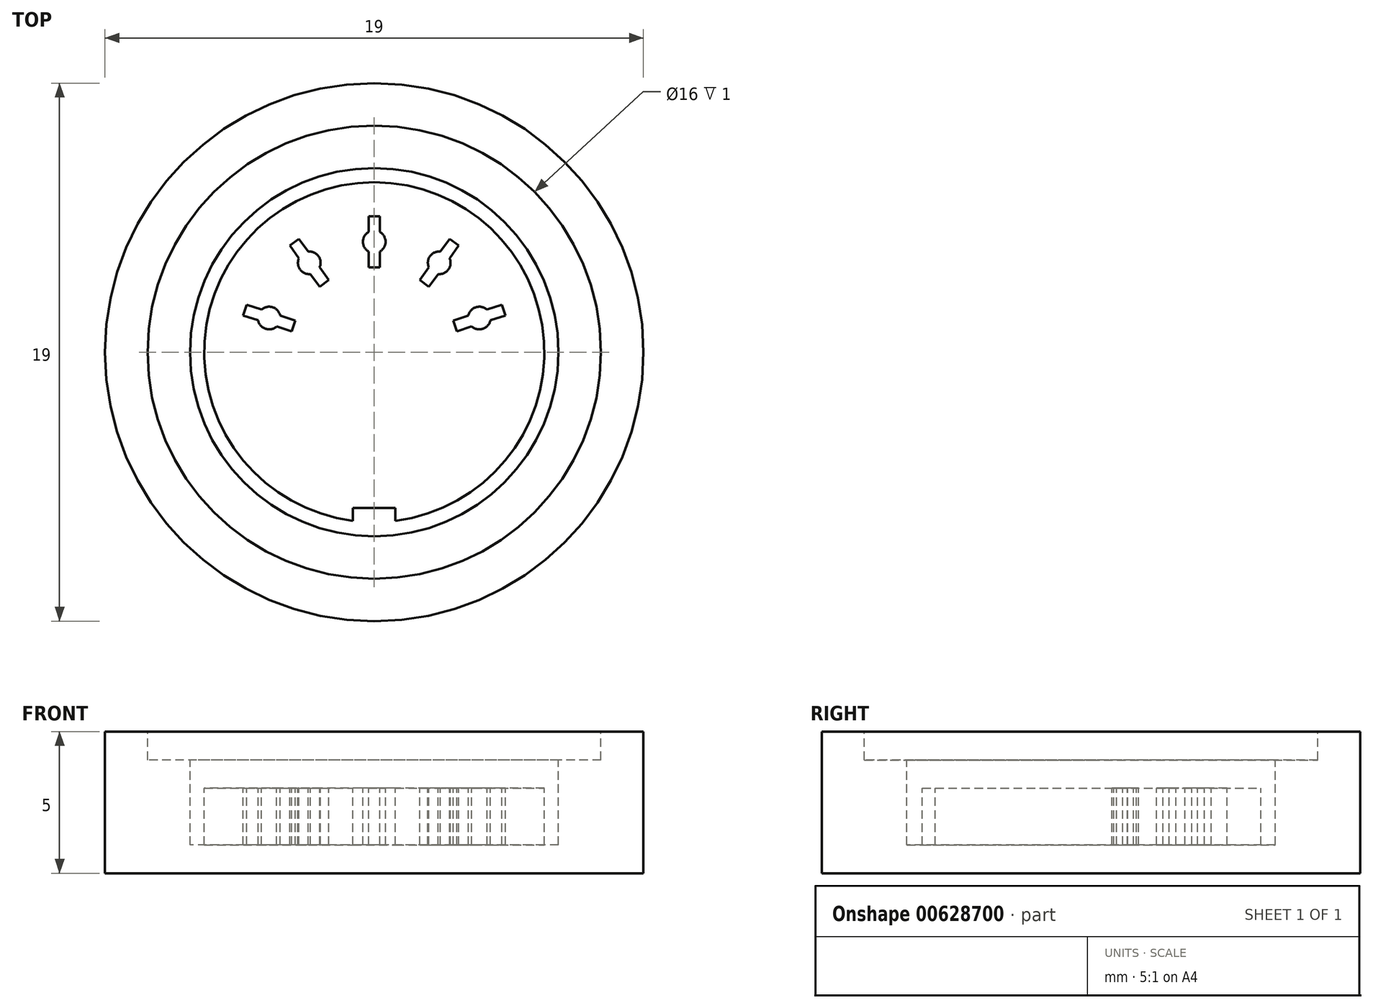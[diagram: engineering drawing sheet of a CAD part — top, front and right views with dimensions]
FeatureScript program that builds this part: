
annotation { "Feature Type Name" : "Feature", "Feature Type Description" : "" }
export const myFeature = defineFeature(function(context is Context, id is Id, definition is map)
    precondition{}
    {
        {
            var Q0;
            Q0=qCreatedBy(makeId("Top.planeOp"),FACE);
            var sketch = newSketch(context, id + "F0", { "sketchPlane" : qUnion([Q0])});
            skCircle(sketch, "E0", {"center": v(0, 0) * mm, "radius": 9.5 * mm});
            skSolve(sketch);
        }
        {
            var Q0;
            Q0 = qSketchRegion(id + "F0", true);
            extrude(context, id + "F1", {"entities" : qUnion([Q0]), "endBound" : BoundingType.SYMMETRIC, "depth" : 5 * mm, "offsetDistance" : 25 * mm});
        }
        {
            var Q0;
            Q0=makeQuery(id+"F1.opExtrude","CAP_FACE",FACE,{"disambiguationData":[OSD([sQuery(id+"F0.wireOp",EDGE,"E0")])],"isStart":false});
            var sketch = newSketch(context, id + "F2", { "sketchPlane" : qUnion([Q0])});
            skCircle(sketch, "E1", {"center": v(0, 0) * mm, "radius": 6.5 * mm});
            skArc(sketch, "E2", {"start": v(0.75, -5.95) * mm, "mid": v(0, 6) * mm, "end": v(-0.75, -5.95) * mm});
            skLineSegment(sketch, "E3", {"start": v(-0.75, -5.95) * mm, "end": v(-0.75, -5.5) * mm});
            skLineSegment(sketch, "E4", {"start": v(-0.75, -5.5) * mm, "end": v(0.75, -5.5) * mm});
            skLineSegment(sketch, "E5", {"start": v(0.75, -5.5) * mm, "end": v(0.75, -5.95) * mm});
            skLineSegment(sketch, "E6.bottom", {"start": v(0.2, 3) * mm, "end": v(-0.2, 3) * mm});
            skLineSegment(sketch, "E6.top", {"start": v(0.2, 4.8) * mm, "end": v(-0.2, 4.8) * mm});
            skLineSegment(sketch, "E6.left", {"start": v(0.2, 3) * mm, "end": v(0.2, 3.55) * mm});
            skLineSegment(sketch, "E6.right", {"start": v(-0.2, 3) * mm, "end": v(-0.2, 3.55) * mm});
            skPoint(sketch, "E6.middle", {"position": v(0, 3.9) * mm});
            skArc(sketch, "E7", {"start": v(-0.2, 4.25) * mm, "mid": v(-0.4, 3.9) * mm, "end": v(-0.2, 3.55) * mm});
            skLineSegment(sketch, "E8.trimOffspring", {"start": v(0.2, 4.25) * mm, "end": v(0.2, 4.8) * mm});
            skLineSegment(sketch, "E9.trimOffspring", {"start": v(-0.2, 4.25) * mm, "end": v(-0.2, 4.8) * mm});
            skArc(sketch, "E10.trimOffspring", {"start": v(0.2, 3.55) * mm, "mid": v(0.4, 3.9) * mm, "end": v(0.2, 4.25) * mm});
            skLineSegment(sketch, "E11.1.0", {"start": v(-1.93, 2.3) * mm, "end": v(-2.25, 2.76) * mm});
            skArc(sketch, "E11.1.1", {"start": v(-2.66, 3.32) * mm, "mid": v(-2.62, 2.92) * mm, "end": v(-2.25, 2.76) * mm});
            skLineSegment(sketch, "E11.1.2", {"start": v(-2.66, 3.32) * mm, "end": v(-2.98, 3.77) * mm});
            skLineSegment(sketch, "E11.1.3", {"start": v(-2.66, 4) * mm, "end": v(-2.98, 3.77) * mm});
            skLineSegment(sketch, "E11.1.4", {"start": v(-2.33, 3.55) * mm, "end": v(-2.66, 4) * mm});
            skArc(sketch, "E11.1.5", {"start": v(-1.93, 3) * mm, "mid": v(-1.97, 3.4) * mm, "end": v(-2.33, 3.55) * mm});
            skLineSegment(sketch, "E11.1.6", {"start": v(-1.6, 2.54) * mm, "end": v(-1.93, 3) * mm});
            skLineSegment(sketch, "E11.1.7", {"start": v(-1.6, 2.54) * mm, "end": v(-1.93, 2.3) * mm});
            skLineSegment(sketch, "E11.2.0", {"start": v(-2.91, 0.74) * mm, "end": v(-3.44, 0.9) * mm});
            skArc(sketch, "E11.2.1", {"start": v(-4.1, 1.12) * mm, "mid": v(-3.83, 0.82) * mm, "end": v(-3.44, 0.9) * mm});
            skLineSegment(sketch, "E11.2.2", {"start": v(-4.1, 1.12) * mm, "end": v(-4.63, 1.3) * mm});
            skLineSegment(sketch, "E11.2.3", {"start": v(-4.5, 1.67) * mm, "end": v(-4.63, 1.3) * mm});
            skLineSegment(sketch, "E11.2.4", {"start": v(-3.98, 1.5) * mm, "end": v(-4.5, 1.67) * mm});
            skArc(sketch, "E11.2.5", {"start": v(-3.32, 1.29) * mm, "mid": v(-3.59, 1.59) * mm, "end": v(-3.98, 1.5) * mm});
            skLineSegment(sketch, "E11.2.6", {"start": v(-2.8, 1.12) * mm, "end": v(-3.32, 1.29) * mm});
            skLineSegment(sketch, "E11.2.7", {"start": v(-2.8, 1.12) * mm, "end": v(-2.91, 0.74) * mm});
            skLineSegment(sketch, "E11.8.0", {"start": v(2.8, 1.12) * mm, "end": v(3.32, 1.29) * mm});
            skArc(sketch, "E11.8.1", {"start": v(3.98, 1.5) * mm, "mid": v(3.59, 1.59) * mm, "end": v(3.32, 1.29) * mm});
            skLineSegment(sketch, "E11.8.2", {"start": v(3.98, 1.5) * mm, "end": v(4.5, 1.67) * mm});
            skLineSegment(sketch, "E11.8.3", {"start": v(4.63, 1.3) * mm, "end": v(4.5, 1.67) * mm});
            skLineSegment(sketch, "E11.8.4", {"start": v(4.1, 1.12) * mm, "end": v(4.63, 1.3) * mm});
            skArc(sketch, "E11.8.5", {"start": v(3.44, 0.9) * mm, "mid": v(3.83, 0.82) * mm, "end": v(4.1, 1.12) * mm});
            skLineSegment(sketch, "E11.8.6", {"start": v(2.91, 0.74) * mm, "end": v(3.44, 0.9) * mm});
            skLineSegment(sketch, "E11.8.7", {"start": v(2.91, 0.74) * mm, "end": v(2.8, 1.12) * mm});
            skLineSegment(sketch, "E11.9.0", {"start": v(1.6, 2.54) * mm, "end": v(1.93, 3) * mm});
            skArc(sketch, "E11.9.1", {"start": v(2.33, 3.55) * mm, "mid": v(1.97, 3.4) * mm, "end": v(1.93, 3) * mm});
            skLineSegment(sketch, "E11.9.2", {"start": v(2.33, 3.55) * mm, "end": v(2.66, 4) * mm});
            skLineSegment(sketch, "E11.9.3", {"start": v(2.98, 3.77) * mm, "end": v(2.66, 4) * mm});
            skLineSegment(sketch, "E11.9.4", {"start": v(2.66, 3.32) * mm, "end": v(2.98, 3.77) * mm});
            skArc(sketch, "E11.9.5", {"start": v(2.25, 2.76) * mm, "mid": v(2.62, 2.92) * mm, "end": v(2.66, 3.32) * mm});
            skLineSegment(sketch, "E11.9.6", {"start": v(1.93, 2.3) * mm, "end": v(2.25, 2.76) * mm});
            skLineSegment(sketch, "E11.9.7", {"start": v(1.93, 2.3) * mm, "end": v(1.6, 2.54) * mm});
            skSolve(sketch);
        }
        {
            var Q0;
            Q0 = qSketchRegion(id + "F2", true);
            var Q1;
            Q1=makeQuery(id+"F2.imprint","IMPRINT",FACE,{"disambiguationData":[TD([[makeQuery(id+"F2.imprint","IMPRINT",EDGE,{"derivedFrom":sQuery(id+"F2.wireOp",EDGE,"E11.2.0")}),-1.0]])]});
            var Q2;
            Q2=makeQuery(id+"F2.imprint","IMPRINT",FACE,{"disambiguationData":[TD([[makeQuery(id+"F2.imprint","IMPRINT",EDGE,{"derivedFrom":sQuery(id+"F2.wireOp",EDGE,"E11.1.0")}),-1.0]])]});
            var Q3;
            Q3=makeQuery(id+"F2.imprint","IMPRINT",FACE,{"disambiguationData":[TD([[makeQuery(id+"F2.imprint","IMPRINT",EDGE,{"derivedFrom":sQuery(id+"F2.wireOp",EDGE,"E6.bottom")}),-1.0]])]});
            var Q4;
            Q4=makeQuery(id+"F2.imprint","IMPRINT",FACE,{"disambiguationData":[TD([[makeQuery(id+"F2.imprint","IMPRINT",EDGE,{"derivedFrom":sQuery(id+"F2.wireOp",EDGE,"E11.9.0")}),-1.0]])]});
            var Q5;
            Q5=makeQuery(id+"F2.imprint","IMPRINT",FACE,{"disambiguationData":[TD([[makeQuery(id+"F2.imprint","IMPRINT",EDGE,{"derivedFrom":sQuery(id+"F2.wireOp",EDGE,"E11.8.0")}),-1.0]])]});
            extrude(context, id + "F3", {"entities" : qUnion([Q0, Q1, Q2, Q3, Q4, Q5]), "operationType" : NewBodyOperationType.REMOVE, "oppositeDirection" : true, "depth" : 4 * mm, "offsetDistance" : 25 * mm});
        }
        {
            var Q0;
            Q0=makeQuery(id+"F3.boolean.opBoolean","SPLIT",FACE,{"disambiguationData":[TD([makeQuery(id+"F3.opExtrude","SWEPT_FACE",FACE,{"disambiguationData":[OSD([sQuery(id+"F2.wireOp",EDGE,"E2")])]})])],"derivedFrom":makeQuery(id+"F1.opExtrude","CAP_FACE",FACE,{"disambiguationData":[OSD([sQuery(id+"F0.wireOp",EDGE,"E0")])],"isStart":false})});
            var sketch = newSketch(context, id + "F4", { "sketchPlane" : qUnion([Q0])});
            skCircle(sketch, "E12", {"center": v(0, 0) * mm, "radius": 6 * mm});
            skSolve(sketch);
        }
        {
            var Q0;
            Q0 = qSketchRegion(id + "F4", true);
            extrude(context, id + "F5", {"entities" : qUnion([Q0]), "operationType" : NewBodyOperationType.REMOVE, "oppositeDirection" : true, "depth" : 2 * mm, "offsetDistance" : 25 * mm});
        }
        {
            var Q0;
            {var subQ0=sQuery(id+"F0.wireOp",EDGE,"E0");Q0=makeQuery(id+"F3.boolean.opBoolean","SPLIT",FACE,{"disambiguationData":[TD([makeQuery(id+"F1.opExtrude","SWEPT_FACE",FACE,{"disambiguationData":[OSD([subQ0])]})])],"derivedFrom":makeQuery(id+"F1.opExtrude","CAP_FACE",FACE,{"disambiguationData":[OSD([subQ0])],"isStart":false})});}
            var sketch = newSketch(context, id + "F6", { "sketchPlane" : qUnion([Q0])});
            skCircle(sketch, "E13", {"center": v(0, 0) * mm, "radius": 8 * mm});
            skSolve(sketch);
        }
        {
            var Q0;
            Q0 = qSketchRegion(id + "F6", true);
            extrude(context, id + "F7", {"entities" : qUnion([Q0]), "operationType" : NewBodyOperationType.REMOVE, "oppositeDirection" : true, "depth" : 1 * mm, "offsetDistance" : 25 * mm});
        }
    });
